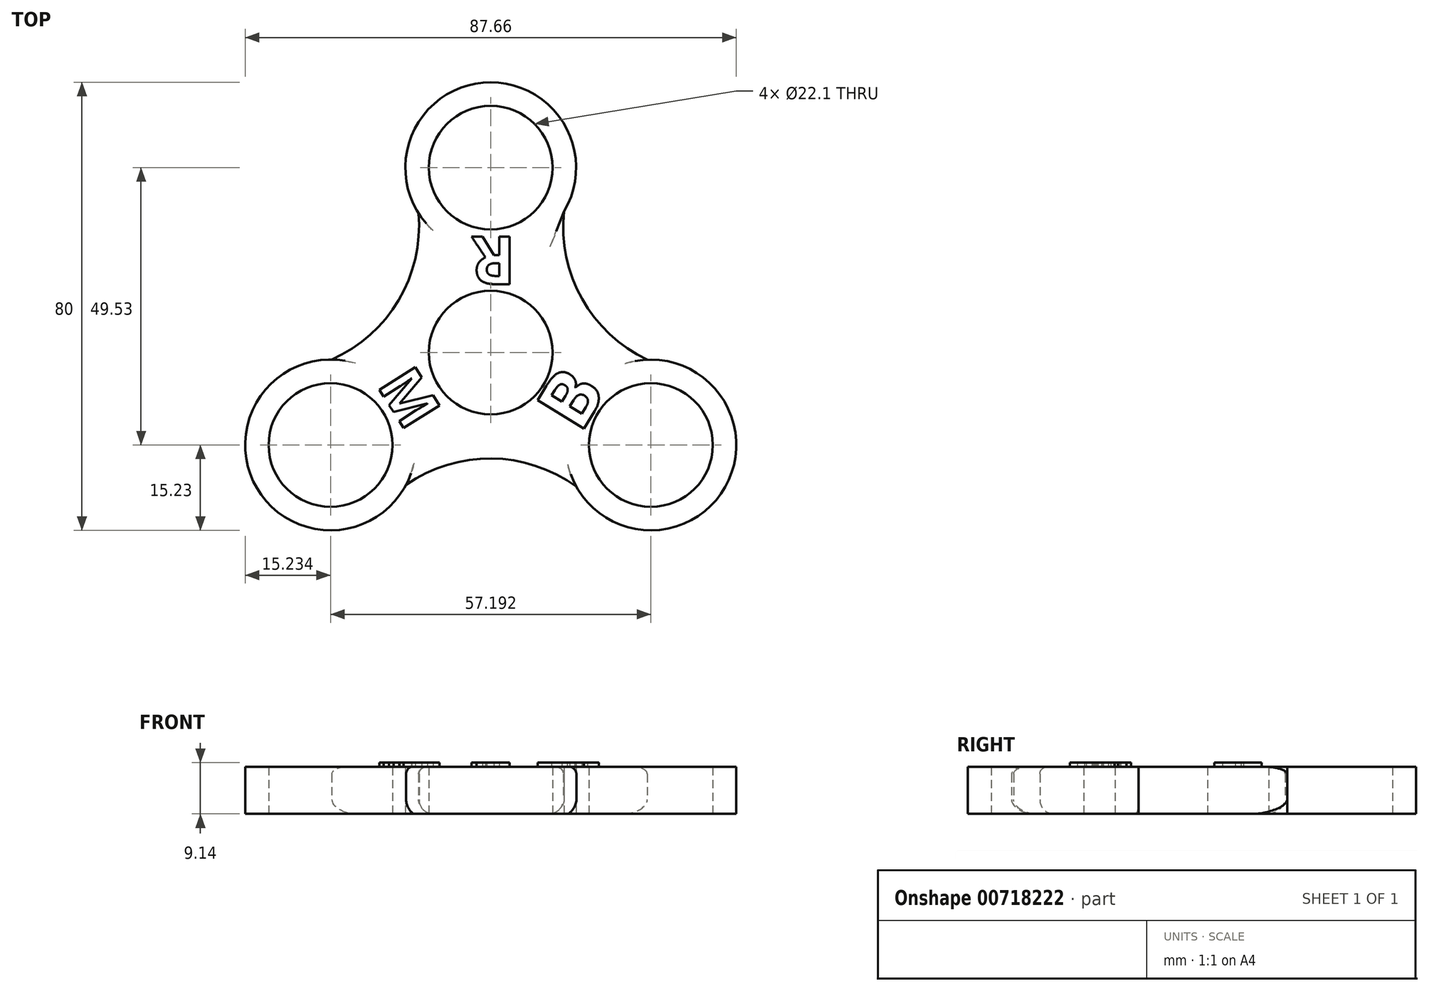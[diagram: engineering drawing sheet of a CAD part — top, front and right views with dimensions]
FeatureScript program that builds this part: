
annotation { "Feature Type Name" : "Feature", "Feature Type Description" : "" }
export const myFeature = defineFeature(function(context is Context, id is Id, definition is map)
    precondition{}
    {
        {
            var Q0;
            Q0=qCreatedBy(makeId("Top.planeOp"),FACE);
            var sketch = newSketch(context, id + "F0", { "sketchPlane" : qUnion([Q0])});
            skCircle(sketch, "E0", {"center": v(0, 0) * mm, "radius": 11.05 * mm});
            skLineSegment(sketch, "E1", {"start": v(0, 0) * mm, "end": v(0, 33.02) * mm});
            skCircle(sketch, "E2", {"center": v(0, 33.02) * mm, "radius": 11.05 * mm});
            skCircle(sketch, "E3.1.0", {"center": v(-28.6, -16.5) * mm, "radius": 11.05 * mm});
            skCircle(sketch, "E3.2.0", {"center": v(28.6, -16.51) * mm, "radius": 11.05 * mm});
            skArc(sketch, "E4", {"start": v(13.1, 25.24) * mm, "mid": v(-0.22, 48.26) * mm, "end": v(-12.88, 24.87) * mm});
            skArc(sketch, "E5.1.0", {"start": v(-28.37, -1.26) * mm, "mid": v(-41.7, -24.28) * mm, "end": v(-15.1, -23.6) * mm});
            skArc(sketch, "E5.2.0", {"start": v(15.3, -23.95) * mm, "mid": v(41.9, -23.93) * mm, "end": v(27.96, -1.27) * mm});
            skArc(sketch, "E6", {"start": v(15.3, -23.95) * mm, "mid": v(0.15, -18.91) * mm, "end": v(-15.1, -23.6) * mm});
            skArc(sketch, "E7.1.0", {"start": v(13.1, 25.22) * mm, "mid": v(16.3, 9.6) * mm, "end": v(27.98, -1.29) * mm});
            skArc(sketch, "E7.2.0", {"start": v(-28.4, -1.27) * mm, "mid": v(-16.46, 9.32) * mm, "end": v(-12.88, 24.88) * mm});
            skLineSegment(sketch, "E8", {"start": v(13.1, 25.22) * mm, "end": v(13.1, 25.24) * mm});
            skSolve(sketch);
        }
        {
            var Q0;
            Q0=makeQuery(id+"F0.imprint","IMPRINT",FACE,{"disambiguationData":[TD([[makeQuery(id+"F0.imprint","IMPRINT",EDGE,{"derivedFrom":sQuery(id+"F0.wireOp",EDGE,"E0")}),-1.0]])]});
            extrude(context, id + "F1", {"entities" : qUnion([Q0]), "depth" : 8.38 * mm, "offsetDistance" : 25.4 * mm});
        }
        {
            var Q0;
            Q0=makeQuery(id+"F1.opExtrude","CAP_FACE",FACE,{"disambiguationData":[OSD([sQuery(id+"F0.wireOp",EDGE,"E0"),sQuery(id+"F0.wireOp",EDGE,"E2"),sQuery(id+"F0.wireOp",EDGE,"E3.1.0"),sQuery(id+"F0.wireOp",EDGE,"E3.2.0"),sQuery(id+"F0.wireOp",EDGE,"E4"),sQuery(id+"F0.wireOp",EDGE,"E5.1.0"),sQuery(id+"F0.wireOp",EDGE,"E5.2.0"),sQuery(id+"F0.wireOp",EDGE,"E6"),sQuery(id+"F0.wireOp",EDGE,"E7.1.0"),sQuery(id+"F0.wireOp",EDGE,"E7.2.0"),sQuery(id+"F0.wireOp",EDGE,"E8")])],"isStart":false});
            var sketch = newSketch(context, id + "F2", { "sketchPlane" : qUnion([Q0])});
            skText(sketch, "E9", { "text": "M", "fontName": "OpenSans-Bold.ttf"});
            skText(sketch, "E10", { "text": "B", "fontName": "OpenSans-Bold.ttf"});
            skText(sketch, "E11", { "text": "R", "fontName": "OpenSans-Bold.ttf"});
            const initialGuessF2  = {"E9": [-0.02036, -0.00586, 0.5351, -0.8448, 0.00762], "E10": [0.01603, -0.01462, 0.519, 0.85477, 0.0098], "E11": [0.00442, 0.02069, -1, 0, 0.00856]};
            skSetInitialGuess(sketch, initialGuessF2);
            skSolve(sketch);
        }
        {
            var Q0;
            Q0 = qSketchRegion(id + "F2", true);
            extrude(context, id + "F3", {"entities" : qUnion([Q0]), "operationType" : NewBodyOperationType.ADD, "depth" : 0.76 * mm, "offsetDistance" : 25.4 * mm});
        }
        {
            var Q0;
            Q0=makeQuery(id+"F1.opExtrude","CAP_EDGE",EDGE,{"disambiguationData":[OSD([sQuery(id+"F0.wireOp",EDGE,"E6")])],"isStart":false});
            var Q1;
            Q1=makeQuery(id+"F1.opExtrude","CAP_EDGE",EDGE,{"disambiguationData":[OSD([sQuery(id+"F0.wireOp",EDGE,"E7.1.0")])],"isStart":false});
            var Q2;
            Q2=makeQuery(id+"F1.opExtrude","CAP_EDGE",EDGE,{"disambiguationData":[OSD([sQuery(id+"F0.wireOp",EDGE,"E7.2.0")])],"isStart":false});
            fillet(context, id + "F4", {"entities" : qUnion([Q0, Q1, Q2]), "radius" : 1.27 * mm, "allowEdgeOverflow" : false});
        }
        {
            var Q0;
            Q0=makeQuery(id+"F1.opExtrude","CAP_EDGE",EDGE,{"disambiguationData":[OSD([sQuery(id+"F0.wireOp",EDGE,"E7.2.0")])],"isStart":true});
            var Q1;
            Q1=makeQuery(id+"F1.opExtrude","CAP_EDGE",EDGE,{"disambiguationData":[OSD([sQuery(id+"F0.wireOp",EDGE,"E6")])],"isStart":true});
            var Q2;
            Q2=makeQuery(id+"F1.opExtrude","CAP_EDGE",EDGE,{"disambiguationData":[OSD([sQuery(id+"F0.wireOp",EDGE,"E7.1.0")])],"isStart":true});
            fillet(context, id + "F5", {"entities" : qUnion([Q0, Q1, Q2]), "radius" : 2.54 * mm, "tangentPropagation" : true, "allowEdgeOverflow" : false});
        }
    });
